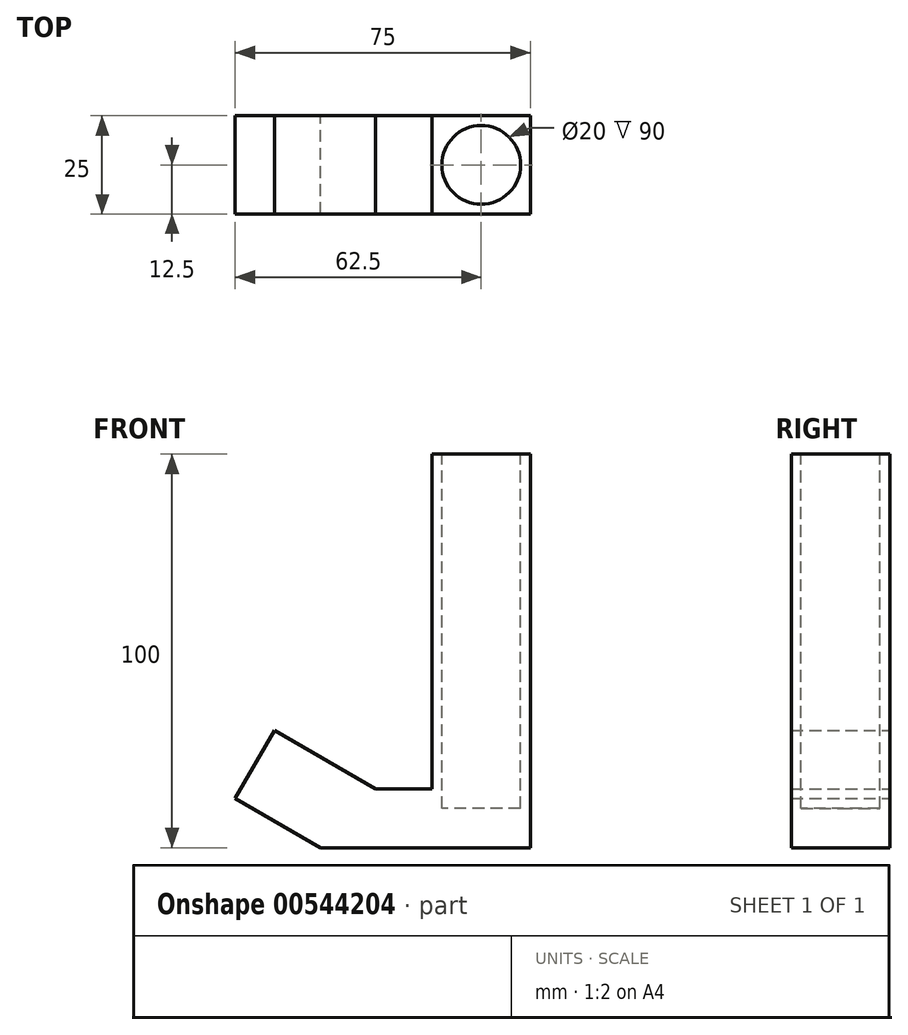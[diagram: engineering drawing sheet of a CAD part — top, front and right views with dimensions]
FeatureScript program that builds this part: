
annotation { "Feature Type Name" : "Feature", "Feature Type Description" : "" }
export const myFeature = defineFeature(function(context is Context, id is Id, definition is map)
    precondition{}
    {
        {
            var Q0;
            Q0=qCreatedBy(makeId("Front.planeOp"),FACE);
            var sketch = newSketch(context, id + "F0", { "sketchPlane" : qUnion([Q0])});
            skLineSegment(sketch, "E0", {"start": v(0, 0) * mm, "end": v(-10, -17.32) * mm});
            skLineSegment(sketch, "E1", {"start": v(-10, -17.32) * mm, "end": v(-10, -17.32) * mm});
            skLineSegment(sketch, "E2", {"start": v(11.65, -29.82) * mm, "end": v(-10, -17.32) * mm});
            skLineSegment(sketch, "E3", {"start": v(11.65, -29.82) * mm, "end": v(65, -29.82) * mm});
            skLineSegment(sketch, "E4", {"start": v(65, -29.82) * mm, "end": v(65, 70.18) * mm});
            skLineSegment(sketch, "E5", {"start": v(65, 70.18) * mm, "end": v(40, 70.18) * mm});
            skLineSegment(sketch, "E6", {"start": v(40, 70.18) * mm, "end": v(40, -14.82) * mm});
            skLineSegment(sketch, "E7", {"start": v(40, -14.82) * mm, "end": v(25.67, -14.82) * mm});
            skLineSegment(sketch, "E8", {"start": v(25.67, -14.82) * mm, "end": v(0, 0) * mm});
            skSolve(sketch);
        }
        {
            var Q0;
            Q0=makeQuery(id+"F0.imprint","IMPRINT",FACE,{"disambiguationData":[TD([[makeQuery(id+"F0.imprint","IMPRINT",EDGE,{"derivedFrom":sQuery(id+"F0.wireOp",EDGE,"E0")}),1.0]])]});
            extrude(context, id + "F1", {"entities" : qUnion([Q0]), "depth" : 12.5 * mm, "offsetDistance" : 25 * mm, "hasSecondDirection" : true, "secondDirectionOppositeDirection" : true, "secondDirectionDepth" : 12.5 * mm});
        }
        {
            var Q0;
            Q0=makeQuery(id+"F1.opExtrude","SWEPT_FACE",FACE,{"disambiguationData":[OSD([sQuery(id+"F0.wireOp",EDGE,"E5")])]});
            var sketch = newSketch(context, id + "F2", { "sketchPlane" : qUnion([Q0])});
            skCircle(sketch, "E9", {"center": v(52.5, 0) * mm, "radius": 12.5 * mm, "construction": true});
            skCircle(sketch, "E10", {"center": v(52.5, 0) * mm, "radius": 10 * mm});
            skSolve(sketch);
        }
        {
            var Q0;
            Q0=makeQuery(id+"F2.imprint","IMPRINT",FACE,{"disambiguationData":[TD([[makeQuery(id+"F2.imprint","IMPRINT",EDGE,{"derivedFrom":sQuery(id+"F2.wireOp",EDGE,"E10")}),1.0]])]});
            var Q1;
            Q1=sQuery(id+"F2.wireOp",EDGE,"E10");
            extrude(context, id + "F3", {"entities" : qUnion([Q0]), "operationType" : NewBodyOperationType.REMOVE, "surfaceEntities" : qUnion([Q1]), "oppositeDirection" : true, "depth" : 90 * mm, "offsetDistance" : 25 * mm});
        }
    });
